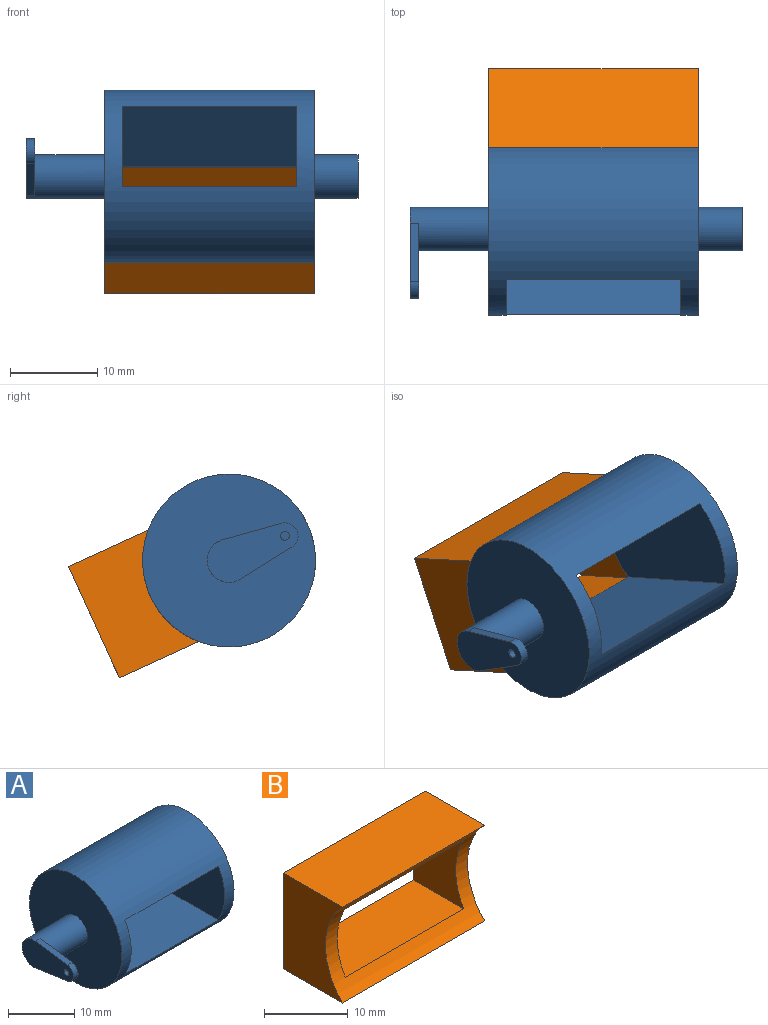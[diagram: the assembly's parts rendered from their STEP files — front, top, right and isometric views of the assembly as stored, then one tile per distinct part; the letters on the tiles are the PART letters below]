
ASSEMBLY  parts=2 mates=1
PART A: 16 faces, bbox 38x19.8x19.8 mm
  f0: cylinder r=9.9mm len=24mm, axis (-1,0,0), area 1073.5mm2, adj f1,f2,f3,f4,f5,f6
  f1: plane 19.8x19.8mm, normal (1,0,0), area 288.2mm2, adj f0,f7
  f2: plane 19.8x19.8mm, normal (-1,0,0), area 288.2mm2, adj f0,f9
  f3: plane 20x17.09mm, normal (0,0,-1), area 341.8mm2, adj f0,f4,f6
  f4: plane 19.8x10mm, normal (1,0,0), area 189.2mm2, adj f0,f3,f5
  f5: plane 20x17.09mm, normal (0,0,1), area 341.8mm2, adj f0,f4,f6
  f6: plane 19.8x10mm, normal (-1,0,0), area 189.2mm2, adj f0,f3,f5
  f7: cylinder r=2.5mm len=5mm, axis (-1,0,0), area 78.5mm2, adj f1,f8
  f8: plane 5x5mm, normal (1,0,0), area 19.6mm2, adj f7
  f9: cylinder r=2.5mm len=9mm, axis (1,0,0), area 134.2mm2, adj f2,f10,f11,f12,f15
  f10: plane 8.14x4.95mm, normal (1,0,0), area 21.2mm2, adj f9,f11,f12,f13,f14
  f11: plane 6.86x1mm, normal (0,-0.14,0.99), area 6.9mm2, adj f9,f10,f13,f15
  f12: plane 6.86x1mm, normal (0,-0.14,-0.99), area 6.9mm2, adj f9,f10,f13,f15
  f13: cylinder r=1.5mm len=2.97mm, axis (1,0,0), area 4.3mm2, adj f10,f11,f12,f15
  f14: cylinder r=0.5mm len=1mm, axis (1,0,0), area 3.1mm2, adj f10,f15
  f15: plane 11x5mm, normal (-1,0,0), area 40.9mm2, adj f9,f11,f12,f13,f14
PART B: 10 faces, bbox 24x10x14 mm
  f0: plane 20x8.46mm, normal (0,0,-1), area 169.1mm2, adj f5,f6,f8,f9
  f1: plane 20x8.46mm, normal (0,0,1), area 169.1mm2, adj f5,f6,f8,f9
  f2: plane 24x10mm, normal (0,0,1), area 240mm2, adj f3,f7,f8,f9
  f3: plane 14x10mm, normal (-1,0,0), area 112mm2, adj f2,f4,f8,f9
  f4: plane 24x10mm, normal (0,0,-1), area 240mm2, adj f3,f7,f8,f9
  f5: plane 10x8.46mm, normal (1,0,0), area 75.4mm2, adj f0,f1,f8,f9
  f6: plane 10x8.46mm, normal (-1,0,0), area 75.4mm2, adj f0,f1,f8,f9
  f7: plane 14x10mm, normal (1,0,0), area 112mm2, adj f2,f4,f8,f9
  f8: plane 24x14mm, normal (0,1,0), area 136mm2, adj f0,f1,f2,f3,f4,f5,f6,f7
  f9: cylinder r=9.9mm len=24mm, axis (-1,0,0), area 163.5mm2, adj f0,f1,f2,f3,f4,f5,f6,f7
PLACE A rot(axis=(-1,0,0),23.8deg) t=(-17,15.55,-6.86)mm
PLACE B rot(axis=(-1,0,0),24.5deg) t=(-17,15.47,-7.06)mm fixed
MATE cylindrical B.f9 <-> A.f0  axis (-1,0,0) through (-7,0,0)mm
